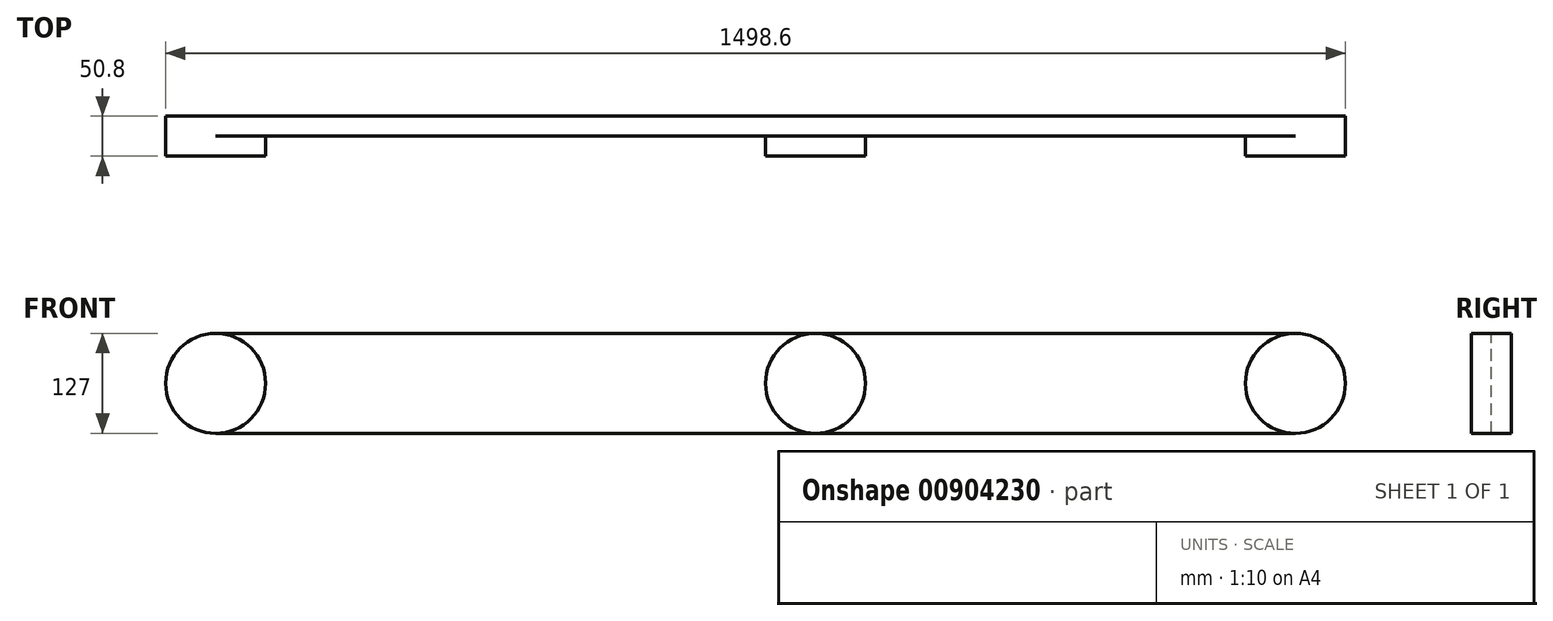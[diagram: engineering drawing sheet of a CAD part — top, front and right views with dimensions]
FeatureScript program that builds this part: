
annotation { "Feature Type Name" : "Feature", "Feature Type Description" : "" }
export const myFeature = defineFeature(function(context is Context, id is Id, definition is map)
    precondition{}
    {
        {
            var Q0;
            Q0=qCreatedBy(makeId("Front.planeOp"),FACE);
            var sketch = newSketch(context, id + "F0", { "sketchPlane" : qUnion([Q0])});
            skLineSegment(sketch, "E0.bottom", {"start": v(0, 0) * mm, "end": v(1371.6, 0) * mm});
            skLineSegment(sketch, "E0.top", {"start": v(0, 127) * mm, "end": v(1371.6, 127) * mm});
            skArc(sketch, "E1", {"start": v(1371.6, 0) * mm, "mid": v(1435.1, 63.5) * mm, "end": v(1371.6, 127) * mm});
            skArc(sketch, "E2", {"start": v(0, 127) * mm, "mid": v(-63.5, 63.5) * mm, "end": v(0, 0) * mm});
            skSolve(sketch);
        }
        {
            var Q0;
            Q0=makeQuery(id+"F0.imprint","IMPRINT",FACE,{"disambiguationData":[TD([[makeQuery(id+"F0.imprint","IMPRINT",EDGE,{"derivedFrom":sQuery(id+"F0.wireOp",EDGE,"E0.bottom")}),1.0]])]});
            extrude(context, id + "F1", {"entities" : qUnion([Q0]), "depth" : 25.4 * mm, "offsetDistance" : 25.4 * mm});
        }
        {
            var Q0;
            Q0=makeQuery(id+"F1.opExtrude","CAP_FACE",FACE,{"disambiguationData":[OSD([sQuery(id+"F0.wireOp",EDGE,"E0.bottom"),sQuery(id+"F0.wireOp",EDGE,"E0.top"),sQuery(id+"F0.wireOp",EDGE,"E1"),sQuery(id+"F0.wireOp",EDGE,"E2")])],"isStart":false});
            var sketch = newSketch(context, id + "F2", { "sketchPlane" : qUnion([Q0])});
            skCircle(sketch, "E3", {"center": v(0, 63.5) * mm, "radius": 63.5 * mm});
            skCircle(sketch, "E4", {"center": v(1371.6, 63.5) * mm, "radius": 63.5 * mm});
            skCircle(sketch, "E5", {"center": v(762, 63.5) * mm, "radius": 63.5 * mm});
            skSolve(sketch);
        }
        {
            var Q0;
            {var subQ0=sQuery(id+"F2.wireOp",EDGE,"E3");var subQ1=makeQuery(id+"F2.imprint","INTERSECT",VERTEX,{"derivedFrom":[makeQuery(id+"F1.opExtrude","CAP_EDGE",EDGE,{"disambiguationData":[OSD([sQuery(id+"F0.wireOp",EDGE,"E0.bottom")])],"isStart":false}),subQ0]});Q0=makeQuery(id+"F2.imprint","IMPRINT",FACE,{"disambiguationData":[TD([[makeQuery(id+"F2.imprint","IMPRINT",EDGE,{"disambiguationData":[TD([[subQ1,1.0]])],"derivedFrom":subQ0}),1.0]])]});}
            var Q1;
            {var subQ0=sQuery(id+"F2.wireOp",EDGE,"E5");var subQ1=makeQuery(id+"F2.imprint","INTERSECT",VERTEX,{"derivedFrom":[makeQuery(id+"F1.opExtrude","CAP_EDGE",EDGE,{"disambiguationData":[OSD([sQuery(id+"F0.wireOp",EDGE,"E0.bottom")])],"isStart":false}),subQ0]});Q1=makeQuery(id+"F2.imprint","IMPRINT",FACE,{"disambiguationData":[TD([[makeQuery(id+"F2.imprint","IMPRINT",EDGE,{"disambiguationData":[TD([[subQ1,1.0]])],"derivedFrom":subQ0}),1.0]])]});}
            var Q2;
            {var subQ0=sQuery(id+"F2.wireOp",EDGE,"E4");var subQ1=makeQuery(id+"F2.imprint","INTERSECT",VERTEX,{"derivedFrom":[makeQuery(id+"F1.opExtrude","CAP_EDGE",EDGE,{"disambiguationData":[OSD([sQuery(id+"F0.wireOp",EDGE,"E0.bottom")])],"isStart":false}),subQ0]});Q2=makeQuery(id+"F2.imprint","IMPRINT",FACE,{"disambiguationData":[TD([[makeQuery(id+"F2.imprint","IMPRINT",EDGE,{"disambiguationData":[TD([[subQ1,-1.0]])],"derivedFrom":subQ0}),1.0]])]});}
            extrude(context, id + "F3", {"entities" : qUnion([Q0, Q1, Q2]), "operationType" : NewBodyOperationType.ADD, "depth" : 25.4 * mm, "offsetDistance" : 25.4 * mm});
        }
    });
